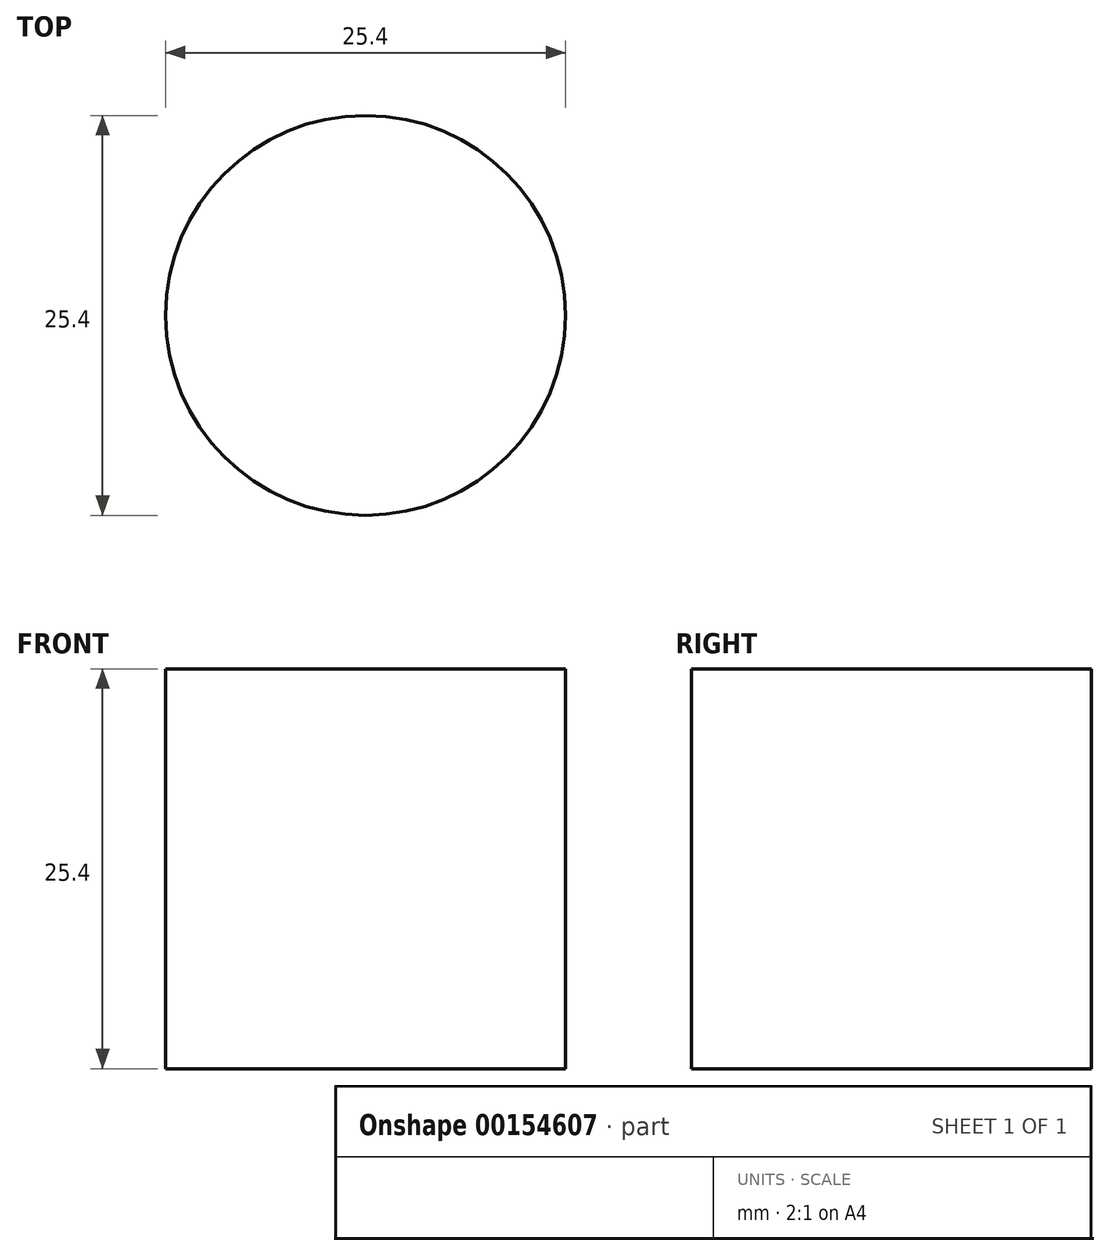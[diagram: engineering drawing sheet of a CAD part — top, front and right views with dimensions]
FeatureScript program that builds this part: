
annotation { "Feature Type Name" : "Feature", "Feature Type Description" : "" }
export const myFeature = defineFeature(function(context is Context, id is Id, definition is map)
    precondition{}
    {
        {
            var Q0;
            Q0=qCreatedBy(makeId("Top.planeOp"),FACE);
            var sketch = newSketch(context, id + "F0", { "sketchPlane" : qUnion([Q0])});
            skCircle(sketch, "E0", {"center": v(0, 0) * mm, "radius": 12.7 * mm});
            skSolve(sketch);
        }
        {
            var Q0;
            Q0=makeQuery(id+"F0.imprint","IMPRINT",FACE,{"disambiguationData":[TD([[makeQuery(id+"F0.imprint","IMPRINT",EDGE,{"derivedFrom":sQuery(id+"F0.wireOp",EDGE,"E0")}),1.0]])]});
            extrude(context, id + "F1", {"entities" : qUnion([Q0]), "depth" : 25.4 * mm});
        }
        {
            var Q0;
            Q0=qCreatedBy(makeId("Right.planeOp"),FACE);
            var sketch = newSketch(context, id + "F2", { "sketchPlane" : qUnion([Q0])});
            skLineSegment(sketch, "E1", {"start": v(19.52, 25.74) * mm, "end": v(0, 0) * mm});
            skSolve(sketch);
        }
        {
            var Q0;
            Q0=sQuery(id+"F2.wireOp",EDGE,"E1");
            var Q1;
            Q1=makeQuery(id+"F1.opExtrude","SWEPT_FACE",FACE,{"disambiguationData":[OSD([sQuery(id+"F0.wireOp",EDGE,"E0")])]});
            revolve(context, id + "F3", {"bodyType" : ToolBodyType.SURFACE, "surfaceEntities" : qUnion([Q0]), "axis" : qUnion([Q1]), "revolveType" : RevolveType.FULL});
        }
    });
